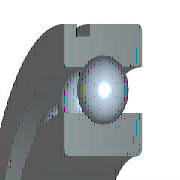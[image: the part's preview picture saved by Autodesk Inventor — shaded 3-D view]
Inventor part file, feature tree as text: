
AUTODESK INVENTOR PART (.ipt)
format: ipt  version: 2015 (Build 190159000, 159)  size: 366,080 bytes
history: native  units: mm (DEFAULTED — no unit token found)
features: sketch x1, other x1, pattern_circular x1
ambient origin geometry x8: Origin, YZ Plane, XZ Plane, XY Plane, X Axis, Y Axis, Z Axis, Center Point
bodies: Solid1 (feature_tree)
feature tree (3):
  sketch  "草图"  dims[d0=3.12mm d17=90.0deg d18=90.0deg d1=0.3mm d2=180.0mm d3=360.0deg d4=0.0mm d5=0.0mm d6=0.0mm d7=30.0mm d8=42.0mm d9=36.0mm d10=40.92mm d11=33.912mm d12=33.912mm d13=33.912mm d14=0.0mm d15=7.0mm d16=7.0mm d19=1.166667mm d20=2.333333mm d22=3.5mm d23=0.0mm d24=0.0mm]
  other  "轴承体"
  pattern_circular  "IDS_ARRAYBALL[SIMPL:T]"  Angle=90.0deg  [1 undecoded]
note: 1 required parameter value undecoded (feature->parameter linkage not recoverable at this tier; creation-order binding heuristic only, values carry confidence <= 0.55)
